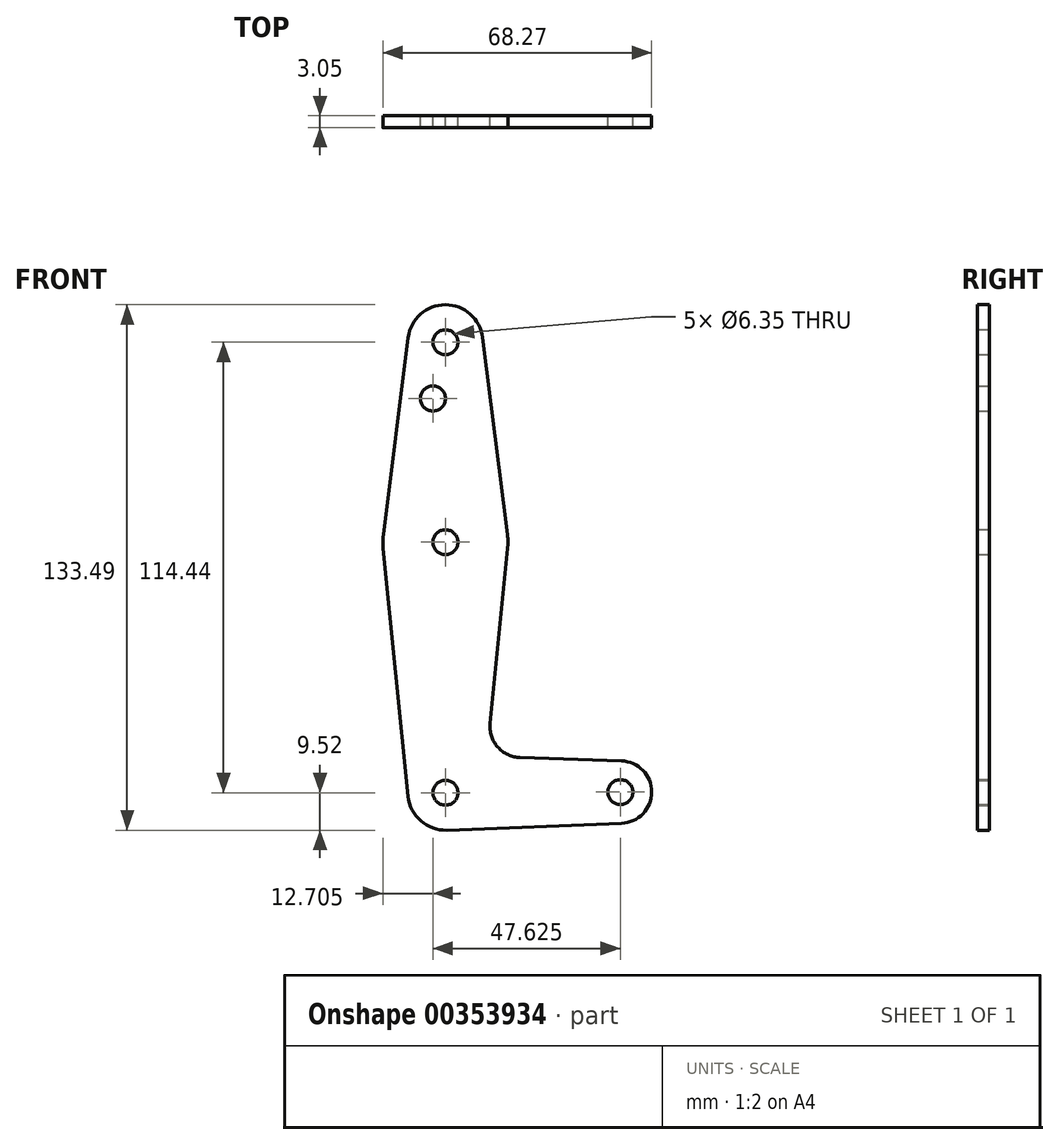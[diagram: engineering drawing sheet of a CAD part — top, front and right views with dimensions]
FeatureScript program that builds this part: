
annotation { "Feature Type Name" : "Feature", "Feature Type Description" : "" }
export const myFeature = defineFeature(function(context is Context, id is Id, definition is map)
    precondition{}
    {
        {
            var Q0;
            Q0=qCreatedBy(makeId("Front.planeOp"),FACE);
            var sketch = newSketch(context, id + "F0", { "sketchPlane" : qUnion([Q0])});
            skLineSegment(sketch, "E0", {"start": v(0, 114.3) * mm, "end": v(0, 63.5) * mm, "construction": true});
            skLineSegment(sketch, "E1", {"start": v(0, 63.5) * mm, "end": v(0, 0) * mm, "construction": true});
            skLineSegment(sketch, "E2", {"start": v(0, 0) * mm, "end": v(44.45, 0) * mm, "construction": true});
            skCircle(sketch, "E3", {"center": v(0, 114.3) * mm, "radius": 9.53 * mm});
            skCircle(sketch, "E4", {"center": v(0, -0.14) * mm, "radius": 9.53 * mm});
            skCircle(sketch, "E5", {"center": v(44.45, 0) * mm, "radius": 7.94 * mm});
            skCircle(sketch, "E6", {"center": v(0, 63.5) * mm, "radius": 15.88 * mm});
            skLineSegment(sketch, "E7", {"start": v(-9.45, 115.5) * mm, "end": v(-15.75, 65.48) * mm});
            skLineSegment(sketch, "E8", {"start": v(9.45, 115.5) * mm, "end": v(15.75, 65.48) * mm});
            skLineSegment(sketch, "E9", {"start": v(-15.8, 61.91) * mm, "end": v(-9.47, -1.1) * mm});
            skLineSegment(sketch, "E10", {"start": v(15.8, 61.92) * mm, "end": v(11.35, 17.5) * mm});
            skLineSegment(sketch, "E11", {"start": v(44.7, 7.93) * mm, "end": v(19, 8.77) * mm});
            skLineSegment(sketch, "E12", {"start": v(44.76, -7.93) * mm, "end": v(0.38, -9.66) * mm});
            skCircle(sketch, "E13", {"center": v(0, 114.3) * mm, "radius": 3.18 * mm});
            skCircle(sketch, "E14", {"center": v(-3.17, 100.03) * mm, "radius": 3.18 * mm});
            skCircle(sketch, "E15", {"center": v(0, 63.5) * mm, "radius": 3.18 * mm});
            skCircle(sketch, "E16", {"center": v(0, -0.14) * mm, "radius": 3.18 * mm});
            skCircle(sketch, "E17", {"center": v(44.45, 0) * mm, "radius": 3.18 * mm});
            skArc(sketch, "E18.filletArc", {"start": v(11.35, 17.5) * mm, "mid": v(13.28, 11.48) * mm, "end": v(19, 8.77) * mm});
            skSolve(sketch);
        }
        {
            var Q0;
            Q0=makeQuery(id+"F0.imprint","IMPRINT",FACE,{"disambiguationData":[TD([[makeQuery(id+"F0.imprint","IMPRINT",EDGE,{"derivedFrom":sQuery(id+"F0.wireOp",EDGE,"E13")}),-1.0]])]});
            var Q1;
            {var subQ0=sQuery(id+"F0.wireOp",EDGE,"E7");Q1=makeQuery(id+"F0.imprint","IMPRINT",FACE,{"disambiguationData":[TD([[makeQuery(id+"F0.imprint","IMPRINT",EDGE,{"derivedFrom":subQ0}),1.0]])]});}
            var Q2;
            {var subQ0=sQuery(id+"F0.wireOp",EDGE,"E9");Q2=makeQuery(id+"F0.imprint","IMPRINT",FACE,{"disambiguationData":[TD([[makeQuery(id+"F0.imprint","IMPRINT",EDGE,{"derivedFrom":subQ0}),1.0]])]});}
            var Q3;
            Q3=makeQuery(id+"F0.imprint","IMPRINT",FACE,{"disambiguationData":[TD([[makeQuery(id+"F0.imprint","IMPRINT",EDGE,{"derivedFrom":sQuery(id+"F0.wireOp",EDGE,"E16")}),-1.0]])]});
            var Q4;
            Q4=makeQuery(id+"F0.imprint","IMPRINT",FACE,{"disambiguationData":[TD([[makeQuery(id+"F0.imprint","IMPRINT",EDGE,{"derivedFrom":sQuery(id+"F0.wireOp",EDGE,"E15")}),-1.0]])]});
            var Q5;
            Q5=makeQuery(id+"F0.imprint","IMPRINT",FACE,{"disambiguationData":[TD([[makeQuery(id+"F0.imprint","IMPRINT",EDGE,{"derivedFrom":sQuery(id+"F0.wireOp",EDGE,"E17")}),-1.0]])]});
            extrude(context, id + "F1", {"entities" : qUnion([Q0, Q1, Q2, Q3, Q4, Q5]), "depth" : 3.05 * mm});
        }
    });
